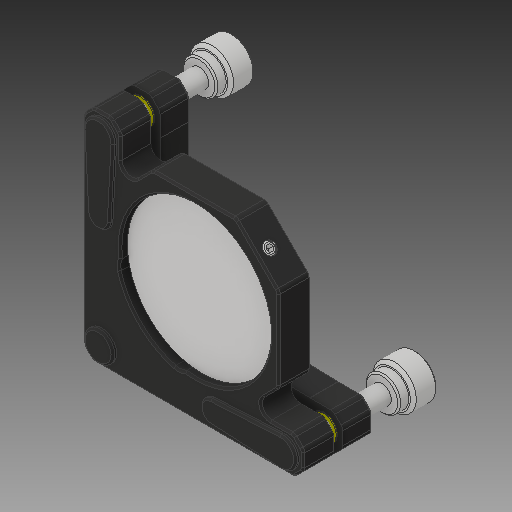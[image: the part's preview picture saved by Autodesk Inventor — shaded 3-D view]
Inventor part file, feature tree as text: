
AUTODESK INVENTOR PART (.ipt)
format: ipt  version: 2017 (Build 210142000, 142)  size: 4,393,472 bytes
history: native  units: in
note: dims shown in document units (in); Inventor stores cm internally (conversion verified against a paired STEP export)
features: other x19, mirror x1
ambient origin geometry x8: Origin, YZ Plane, XZ Plane, XY Plane, X Axis, Y Axis, Z Axis, Center Point
bodies: Solid1 (feature_tree), Solid2 (feature_tree), Solid3 (feature_tree), Solid4 (feature_tree), Solid5 (feature_tree), Solid6 (feature_tree), Solid7 (feature_tree), Solid8 (feature_tree), Solid9 (feature_tree), Solid10 (feature_tree), Solid11 (feature_tree), Solid12 (feature_tree), Solid13 (feature_tree), Solid14 (feature_tree), Solid15 (feature_tree), Solid16 (feature_tree), Solid17 (feature_tree), Solid18 (feature_tree), Solid19 (feature_tree), Solid20 (feature_tree)
feature tree (20):
  other  "6635-002-1-solid1"
  other  "6635-001A-1-solid1"
  other  "1579-006-2-solid1"
  other  "1579-006-3-solid1"
  other  "1579-004-2-solid1"
  other  "1579-004-3-solid1"
  other  "Dowel Pin_AI-1-solid1"
  other  "Dowel Pin_AI-2-solid1"
  other  "W25H042-1-solid1"
  other  "Backup of Ball 5-16-1-solid1"
  other  "Dowel Pin_AI-6-solid1"
  other  "Dowel Pin_AI-7-solid1"
  other  "Dowel Pin_AI-8-solid1"
  other  "km3-1-solid1"
  other  "km3-2-solid1"
  other  "km3-3-solid1"
  other  "Socket Set Screw Half Dog Point_AI-1-solid1"
  mirror  "mirror-1-solid1"
  other  "bushing-1-solid1"
  other  "bushing-2-solid1"
